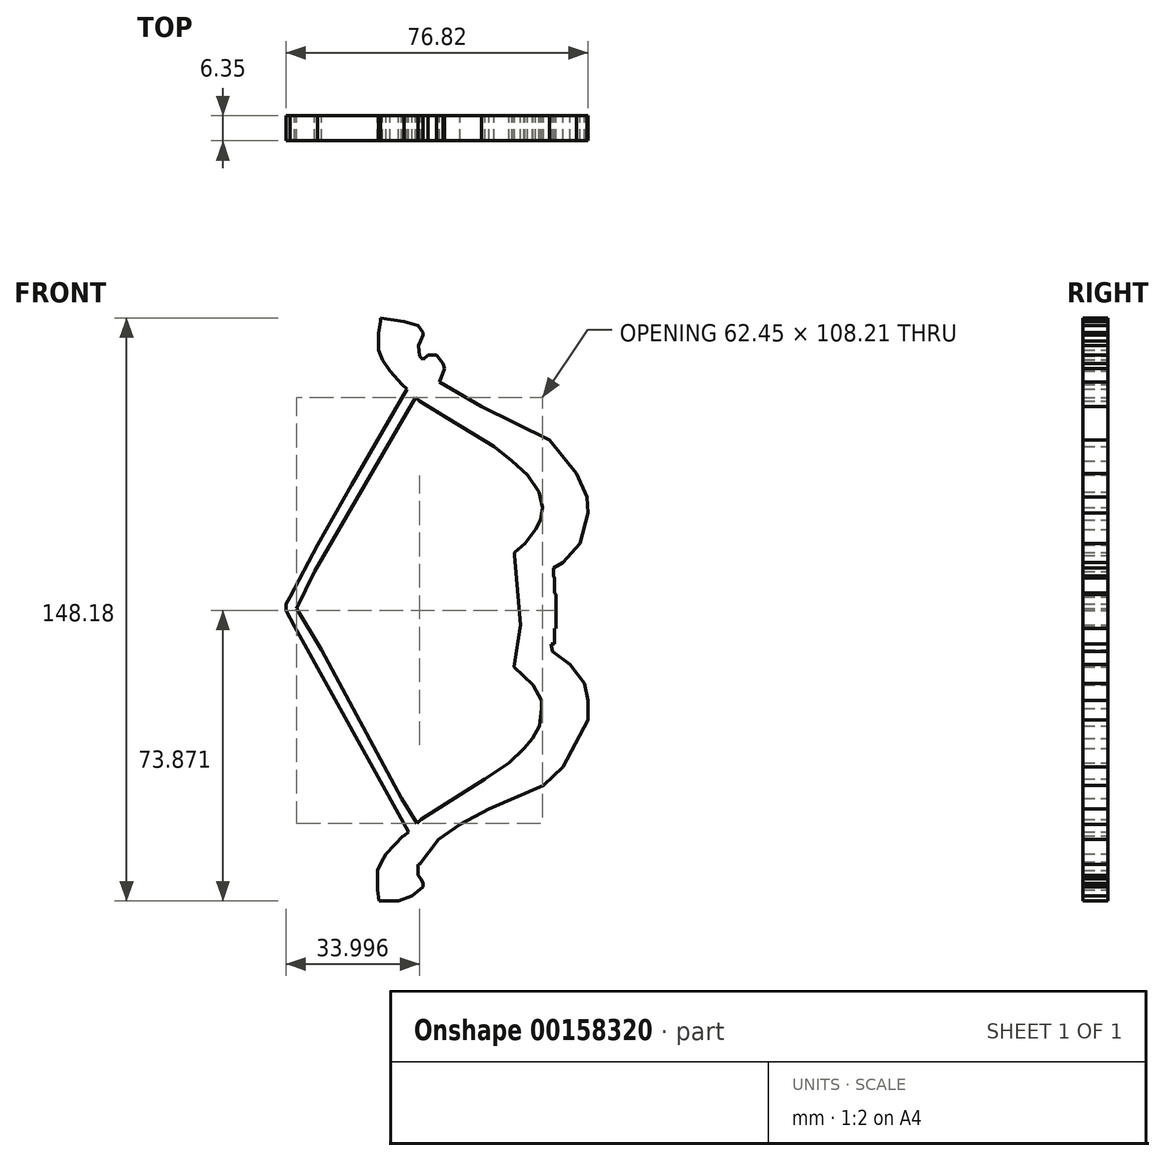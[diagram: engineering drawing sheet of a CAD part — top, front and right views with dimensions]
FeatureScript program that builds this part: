
annotation { "Feature Type Name" : "Feature", "Feature Type Description" : "" }
export const myFeature = defineFeature(function(context is Context, id is Id, definition is map)
    precondition{}
    {
        {
            var Q0;
            Q0=qCreatedBy(makeId("Front.planeOp"),FACE);
            var sketch = newSketch(context, id + "F0", { "sketchPlane" : qUnion([Q0])});
            skLineSegment(sketch, "E0", {"start": v(-35.63, 72.36) * mm, "end": v(-34.3, 70.7) * mm});
            skLineSegment(sketch, "E1", {"start": v(-34.3, 70.7) * mm, "end": v(-34.3, 70.02) * mm});
            skLineSegment(sketch, "E2", {"start": v(-34.3, 70.02) * mm, "end": v(-34.91, 68.5) * mm});
            skLineSegment(sketch, "E3", {"start": v(-34.91, 68.5) * mm, "end": v(-35.48, 67.4) * mm});
            skLineSegment(sketch, "E4", {"start": v(-35.48, 67.4) * mm, "end": v(-35.22, 64.68) * mm});
            skLineSegment(sketch, "E5", {"start": v(-35.22, 64.68) * mm, "end": v(-34.29, 63.73) * mm});
            skLineSegment(sketch, "E6", {"start": v(-34.29, 63.73) * mm, "end": v(-33.04, 64.95) * mm});
            skLineSegment(sketch, "E7", {"start": v(-33.04, 64.95) * mm, "end": v(-30.88, 64.95) * mm});
            skLineSegment(sketch, "E8", {"start": v(-30.88, 64.95) * mm, "end": v(-29.26, 62.74) * mm});
            skLineSegment(sketch, "E9", {"start": v(-29.26, 62.74) * mm, "end": v(-28.9, 61.44) * mm});
            skLineSegment(sketch, "E10", {"start": v(-28.9, 61.44) * mm, "end": v(-30.06, 58.02) * mm});
            skLineSegment(sketch, "E11", {"start": v(-30.06, 58.02) * mm, "end": v(-19.41, 51.84) * mm});
            skLineSegment(sketch, "E12", {"start": v(-19.41, 51.84) * mm, "end": v(-2.22, 43.38) * mm});
            skLineSegment(sketch, "E13", {"start": v(-2.22, 43.38) * mm, "end": v(4.65, 34.8) * mm});
            skLineSegment(sketch, "E14", {"start": v(4.65, 34.8) * mm, "end": v(7.32, 28.82) * mm});
            skLineSegment(sketch, "E15", {"start": v(7.32, 28.82) * mm, "end": v(7.66, 24.79) * mm});
            skLineSegment(sketch, "E16", {"start": v(7.66, 24.79) * mm, "end": v(5.58, 17.02) * mm});
            skLineSegment(sketch, "E17", {"start": v(5.58, 17.02) * mm, "end": v(1.25, 12.27) * mm});
            skLineSegment(sketch, "E18", {"start": v(1.25, 12.27) * mm, "end": v(-1.18, 10.83) * mm});
            skLineSegment(sketch, "E19", {"start": v(-1.18, 10.83) * mm, "end": v(-1.18, 8.8) * mm});
            skLineSegment(sketch, "E20", {"start": v(-1.18, 8.8) * mm, "end": v(-0.93, 8.27) * mm});
            skLineSegment(sketch, "E21", {"start": v(-0.93, 8.27) * mm, "end": v(-0.93, 4.46) * mm});
            skLineSegment(sketch, "E22", {"start": v(-0.93, 4.46) * mm, "end": v(-0.54, 4.1) * mm});
            skLineSegment(sketch, "E23", {"start": v(-0.54, 4.1) * mm, "end": v(-0.54, -3.98) * mm});
            skLineSegment(sketch, "E24", {"start": v(-0.54, -3.98) * mm, "end": v(-0.54, -4.55) * mm});
            skLineSegment(sketch, "E25", {"start": v(-0.96, -4.55) * mm, "end": v(-0.54, -4.55) * mm});
            skLineSegment(sketch, "E26", {"start": v(-0.96, -4.55) * mm, "end": v(-0.96, -8.46) * mm});
            skLineSegment(sketch, "E27", {"start": v(-0.96, -8.46) * mm, "end": v(-1.74, -8.46) * mm});
            skLineSegment(sketch, "E28", {"start": v(-1.74, -8.46) * mm, "end": v(-1.46, -10.38) * mm});
            skLineSegment(sketch, "E29", {"start": v(-1.46, -10.38) * mm, "end": v(2.99, -13.73) * mm});
            skLineSegment(sketch, "E30", {"start": v(2.99, -13.73) * mm, "end": v(6.72, -18.47) * mm});
            skLineSegment(sketch, "E31", {"start": v(6.72, -18.47) * mm, "end": v(7.64, -22.78) * mm});
            skLineSegment(sketch, "E32", {"start": v(7.64, -22.78) * mm, "end": v(7.64, -27.77) * mm});
            skLineSegment(sketch, "E33", {"start": v(7.64, -27.77) * mm, "end": v(1.27, -39.68) * mm});
            skLineSegment(sketch, "E34", {"start": v(1.27, -39.68) * mm, "end": v(-3.69, -44.46) * mm});
            skLineSegment(sketch, "E35", {"start": v(-3.69, -44.46) * mm, "end": v(-17.6, -50.43) * mm});
            skLineSegment(sketch, "E36", {"start": v(-17.6, -50.43) * mm, "end": v(-24.92, -54.34) * mm});
            skLineSegment(sketch, "E37", {"start": v(-24.92, -54.34) * mm, "end": v(-29.96, -57.83) * mm});
            skLineSegment(sketch, "E38", {"start": v(-29.96, -57.83) * mm, "end": v(-30.35, -58.1) * mm});
            skLineSegment(sketch, "E39", {"start": v(-30.35, -58.1) * mm, "end": v(-35.2, -64.49) * mm});
            skLineSegment(sketch, "E40", {"start": v(-35.2, -64.49) * mm, "end": v(-35.54, -64.49) * mm});
            skLineSegment(sketch, "E41", {"start": v(-35.54, -64.49) * mm, "end": v(-35.54, -67.22) * mm});
            skLineSegment(sketch, "E42", {"start": v(-35.54, -67.22) * mm, "end": v(-34.82, -68.12) * mm});
            skLineSegment(sketch, "E43", {"start": v(-34.82, -68.12) * mm, "end": v(-34.34, -69.32) * mm});
            skLineSegment(sketch, "E44", {"start": v(-34.34, -69.32) * mm, "end": v(-34.34, -70.18) * mm});
            skLineSegment(sketch, "E45", {"start": v(-34.34, -70.18) * mm, "end": v(-37.15, -72.5) * mm});
            skLineSegment(sketch, "E46", {"start": v(-37.15, -72.5) * mm, "end": v(-40.56, -73.8) * mm});
            skLineSegment(sketch, "E47", {"start": v(-40.56, -73.8) * mm, "end": v(-45.46, -73.8) * mm});
            skLineSegment(sketch, "E48", {"start": v(-45.46, -73.8) * mm, "end": v(-45.86, -70.9) * mm});
            skLineSegment(sketch, "E49", {"start": v(-45.86, -70.9) * mm, "end": v(-45.86, -66) * mm});
            skLineSegment(sketch, "E50", {"start": v(-45.86, -66) * mm, "end": v(-44.79, -63.86) * mm});
            skLineSegment(sketch, "E51", {"start": v(-44.79, -63.86) * mm, "end": v(-43.71, -61.86) * mm});
            skLineSegment(sketch, "E52", {"start": v(-43.71, -61.86) * mm, "end": v(-39.42, -57.23) * mm});
            skLineSegment(sketch, "E53", {"start": v(-39.42, -57.23) * mm, "end": v(-39.1, -57.23) * mm});
            skLineSegment(sketch, "E54", {"start": v(-39.1, -57.23) * mm, "end": v(-38.03, -56.2) * mm});
            skLineSegment(sketch, "E55", {"start": v(-34.82, -53.12) * mm, "end": v(-18.5, -42.75) * mm});
            skLineSegment(sketch, "E56", {"start": v(-18.5, -42.75) * mm, "end": v(-12.49, -38.74) * mm});
            skLineSegment(sketch, "E57", {"start": v(-12.49, -38.74) * mm, "end": v(-8.63, -35.08) * mm});
            skLineSegment(sketch, "E58", {"start": v(-8.63, -35.08) * mm, "end": v(-6.47, -32.47) * mm});
            skLineSegment(sketch, "E59", {"start": v(-6.47, -32.47) * mm, "end": v(-4.67, -29.26) * mm});
            skLineSegment(sketch, "E60", {"start": v(-4.67, -29.26) * mm, "end": v(-4.22, -24.9) * mm});
            skLineSegment(sketch, "E61", {"start": v(-4.22, -24.9) * mm, "end": v(-4.22, -22.89) * mm});
            skLineSegment(sketch, "E62", {"start": v(-4.22, -22.89) * mm, "end": v(-6.37, -18.84) * mm});
            skLineSegment(sketch, "E63", {"start": v(-6.37, -18.84) * mm, "end": v(-11.15, -14.34) * mm});
            skLineSegment(sketch, "E64", {"start": v(-11.15, -14.34) * mm, "end": v(-9.58, -3.7) * mm});
            skLineSegment(sketch, "E65", {"start": v(-9.58, -3.7) * mm, "end": v(-11.09, 13.97) * mm});
            skLineSegment(sketch, "E66", {"start": v(-11.09, 13.97) * mm, "end": v(-11.09, 14.8) * mm});
            skLineSegment(sketch, "E67", {"start": v(-11.09, 14.8) * mm, "end": v(-8.47, 17) * mm});
            skLineSegment(sketch, "E68", {"start": v(-8.47, 17) * mm, "end": v(-5.73, 20.59) * mm});
            skLineSegment(sketch, "E69", {"start": v(-5.73, 20.59) * mm, "end": v(-4.47, 22.97) * mm});
            skLineSegment(sketch, "E70", {"start": v(-4.47, 22.97) * mm, "end": v(-3.94, 26.25) * mm});
            skLineSegment(sketch, "E71", {"start": v(-3.94, 26.25) * mm, "end": v(-4.83, 30.18) * mm});
            skLineSegment(sketch, "E72", {"start": v(-4.83, 30.18) * mm, "end": v(-7.75, 34.47) * mm});
            skLineSegment(sketch, "E73", {"start": v(-7.75, 34.47) * mm, "end": v(-11.69, 38.05) * mm});
            skLineSegment(sketch, "E74", {"start": v(-11.69, 38.05) * mm, "end": v(-16.33, 41.7) * mm});
            skLineSegment(sketch, "E75", {"start": v(-16.33, 41.7) * mm, "end": v(-21.53, 44.82) * mm});
            skLineSegment(sketch, "E76", {"start": v(-21.53, 44.82) * mm, "end": v(-28.63, 49.18) * mm});
            skLineSegment(sketch, "E77", {"start": v(-28.63, 49.18) * mm, "end": v(-35.25, 53.24) * mm});
            skLineSegment(sketch, "E78", {"start": v(-35.25, 53.24) * mm, "end": v(-36.21, 54.17) * mm});
            skPoint(sketch, "E78.endSnap0", {"position": v(-32.03, 57.4) * mm});
            skLineSegment(sketch, "E79", {"start": v(-39.6, 57.4) * mm, "end": v(-42.65, 60.92) * mm});
            skLineSegment(sketch, "E80", {"start": v(-42.65, 60.92) * mm, "end": v(-44.61, 63.66) * mm});
            skLineSegment(sketch, "E81", {"start": v(-44.61, 63.66) * mm, "end": v(-45.63, 66.16) * mm});
            skLineSegment(sketch, "E82", {"start": v(-45.63, 66.16) * mm, "end": v(-45.63, 70.43) * mm});
            skLineSegment(sketch, "E83", {"start": v(-45.63, 70.43) * mm, "end": v(-45.09, 73.59) * mm});
            skLineSegment(sketch, "E84", {"start": v(-45.09, 73.59) * mm, "end": v(-45.09, 74.37) * mm});
            skLineSegment(sketch, "E85", {"start": v(-45.09, 74.37) * mm, "end": v(-39.19, 73.4) * mm});
            skLineSegment(sketch, "E86", {"start": v(-39.19, 73.4) * mm, "end": v(-35.63, 72.36) * mm});
            skLineSegment(sketch, "E87", {"start": v(-36.21, 54.17) * mm, "end": v(-61.88, 9.98) * mm});
            skPoint(sketch, "E87.startSnap0", {"position": v(-34.68, 54.17) * mm});
            skLineSegment(sketch, "E88", {"start": v(-66.4, 0.49) * mm, "end": v(-60.15, -9.97) * mm});
            skLineSegment(sketch, "E89", {"start": v(-60.15, -9.97) * mm, "end": v(-39.81, -47.71) * mm});
            skLineSegment(sketch, "E90", {"start": v(-39.81, -47.71) * mm, "end": v(-35.79, -54.04) * mm});
            skLineSegment(sketch, "E91", {"start": v(-38.03, -56.2) * mm, "end": v(-66.96, -4.07) * mm});
            skLineSegment(sketch, "E92", {"start": v(-66.96, -4.07) * mm, "end": v(-69.16, 0) * mm});
            skLineSegment(sketch, "E93", {"start": v(-69.16, 0) * mm, "end": v(-69.16, 1.65) * mm});
            skLineSegment(sketch, "E94", {"start": v(-69.16, 1.65) * mm, "end": v(-68.14, 3.42) * mm});
            skLineSegment(sketch, "E95", {"start": v(-68.14, 3.42) * mm, "end": v(-61.13, 16.64) * mm});
            skLineSegment(sketch, "E96", {"start": v(-61.13, 16.64) * mm, "end": v(-52.43, 31.96) * mm});
            skLineSegment(sketch, "E97", {"start": v(-52.43, 31.96) * mm, "end": v(-38.38, 56.23) * mm});
            skPoint(sketch, "E98.orphan", {"position": v(-31.09, 57.88) * mm});
            skPoint(sketch, "E99.end.orphan", {"position": v(-32.98, 56.93) * mm});
            skPoint(sketch, "E100.orphan", {"position": v(-34.12, 55.09) * mm});
            skLineSegment(sketch, "E101.trimOffspring", {"start": v(-38.38, 56.23) * mm, "end": v(-39.6, 57.4) * mm});
            skLineSegment(sketch, "E102", {"start": v(-61.88, 9.98) * mm, "end": v(-66.4, 0.49) * mm});
            skLineSegment(sketch, "E103.trimOffspring", {"start": v(-35.79, -54.04) * mm, "end": v(-34.82, -53.12) * mm});
            skSolve(sketch);
        }
        {
            var Q0;
            Q0 = qSketchRegion(id + "F0", true);
            extrude(context, id + "F1", {"entities" : qUnion([Q0]), "depth" : 6.35 * mm});
        }
    });
